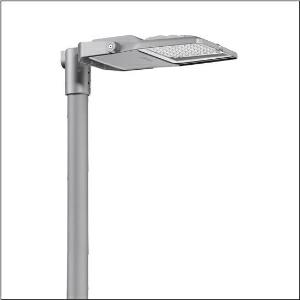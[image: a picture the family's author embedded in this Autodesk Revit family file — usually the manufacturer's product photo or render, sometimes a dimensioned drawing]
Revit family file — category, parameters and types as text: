
# Revit family: floodlight_fl_21_mini___pl52_5xa7775d2d3a_ca02
name_source: partatom
category: Lighting Fixtures
units: mm (PartAtom-declared; Revit-internal decimal feet)

## family parameters
Cut with Voids When Loaded = No
Host = Face
Light Source = No
Part Type = Normal
Room Calculation Point = No
Round Connector Dimension = Use Diameter
Shared = No

## types (1)
- --- (1 x LED, 17840 lm, 142.9 W, 3000K)
    Apparent Load = 143 VA
    CIE Flux Codes = 26 60 98 100 100
    Color Rendering = 70
    Color Temperature = 3000K
    Default Elevation = 1800 mm
    Description = Floodlight FL 21 mini, floodlight, primary light control with lens, of PMMA, primary optical cover: protective disc, of toughened safety glass, transparent, light distribution: PL52, light emission: direct distribution, installation type: surface-mounted, LED, High Power LED, rated luminous flux: 17.840lm, luminous efficacy: 125lm/W, light colour: 730, colour temperature: 3000K, control: flexible luminous flux parameterisation, time-dependent luminous flux control, constant luminous flux control, overheat protection, pre-setting: logarithmic dimming characteristic, with terminal, 6-pole, mains connection: 220..240V, AC, 50/60Hz, start of lifetime: 143W, end of service life: 151W, reduction: 63W, luminaire housing, of diecast aluminium, powder-coated, Siteco® metallic grey (DB 702S), corrosivity category C5 mid according to DIN EN ISO 12944, sealing non-destructively replaceable, please order mast flange separately, mast bracket, of steel, galvanised, powder-coated, Siteco® metallic grey (DB 702S), Smart Interface above, protection rating (complete): IP66, insulation class (complete): insulation class II (safety insulation), certification: CE, ENEC, VDE, protection symbol: D, impact resistance: IK08, permissible operating ambient temperature: -40..+40°C, permissible operating ambient temperature for outdoor applications: -40..+50°C, standard: DIN EN 12944, LABS conformity tested according to VDMA 24364:2018-05, packaging unit: 1 piece

Light Distribution: PL52
    Height = 70 mm
    Lamp = 1 x LED
    Lamp Light Flux = 17840 lm
    Lamp Power = 142.9 W
    Lamp count = 1
    Length = 485 mm
    Luminous efficacy = 125 lm/W
    Manufacturer = Siteco
    ModVariant = No
    Model = 5XA7775D2D3A
    Number of Poles = 1
    OnlyDefault = Yes
    Power Factor = 1
    Product Name = Floodlight FL 21 mini | PL52
    Product group = floodlight | pylon annexe
    ProductGroupID = 6200
    Protection Class = Protection class II
    Protection Degree = IP 66
    RLX_Detail_Level = 1
    RLX_Emergency_Light_Flux = 0 lm
    RLX_Emergency_Type = 0
    RLX_Emergency_Type_DB = No
    RlxData = <blob elided: 101481 chars, md5=73dd159d>
    Socket = socket
    Standby Power = 0 W
    System Light Flux = 17840 lm
    System Power = 143 W
    Type Comments = factory setting: luminous flux: 100 % | dim-lin: 254 | 730 mA
    Type Image = l_1007125.jpg
    URL = http://relux.com
    VarID = @adj_133519
    Voltage = 0 V
    Weight = 0.00 kg
    Width = 337 mm

## geometry (parser evidence)
native form markers: Blend x4, Sweep x14
no freeform markers — native parametric forms only
